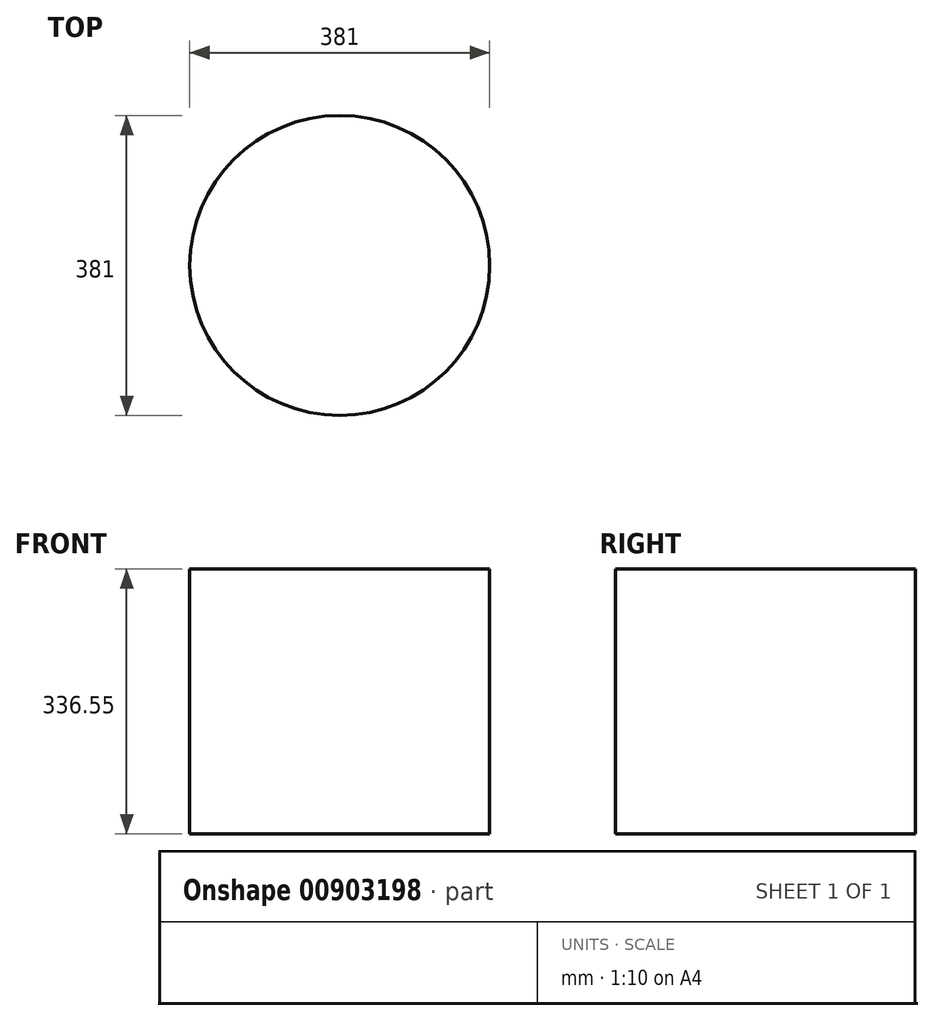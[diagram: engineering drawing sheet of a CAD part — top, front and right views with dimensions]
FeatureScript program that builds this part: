
annotation { "Feature Type Name" : "Feature", "Feature Type Description" : "" }
export const myFeature = defineFeature(function(context is Context, id is Id, definition is map)
    precondition{}
    {
        {
            var Q0;
            Q0=qCreatedBy(makeId("Top.planeOp"),FACE);
            var sketch = newSketch(context, id + "F0", { "sketchPlane" : qUnion([Q0])});
            skCircle(sketch, "E0", {"center": v(0, 0) * mm, "radius": 190.5 * mm});
            skSolve(sketch);
        }
        {
            var Q0;
            Q0 = qSketchRegion(id + "F0", true);
            extrude(context, id + "F1", {"entities" : qUnion([Q0]), "depth" : 336.55 * mm, "offsetDistance" : 25.4 * mm});
        }
    });
